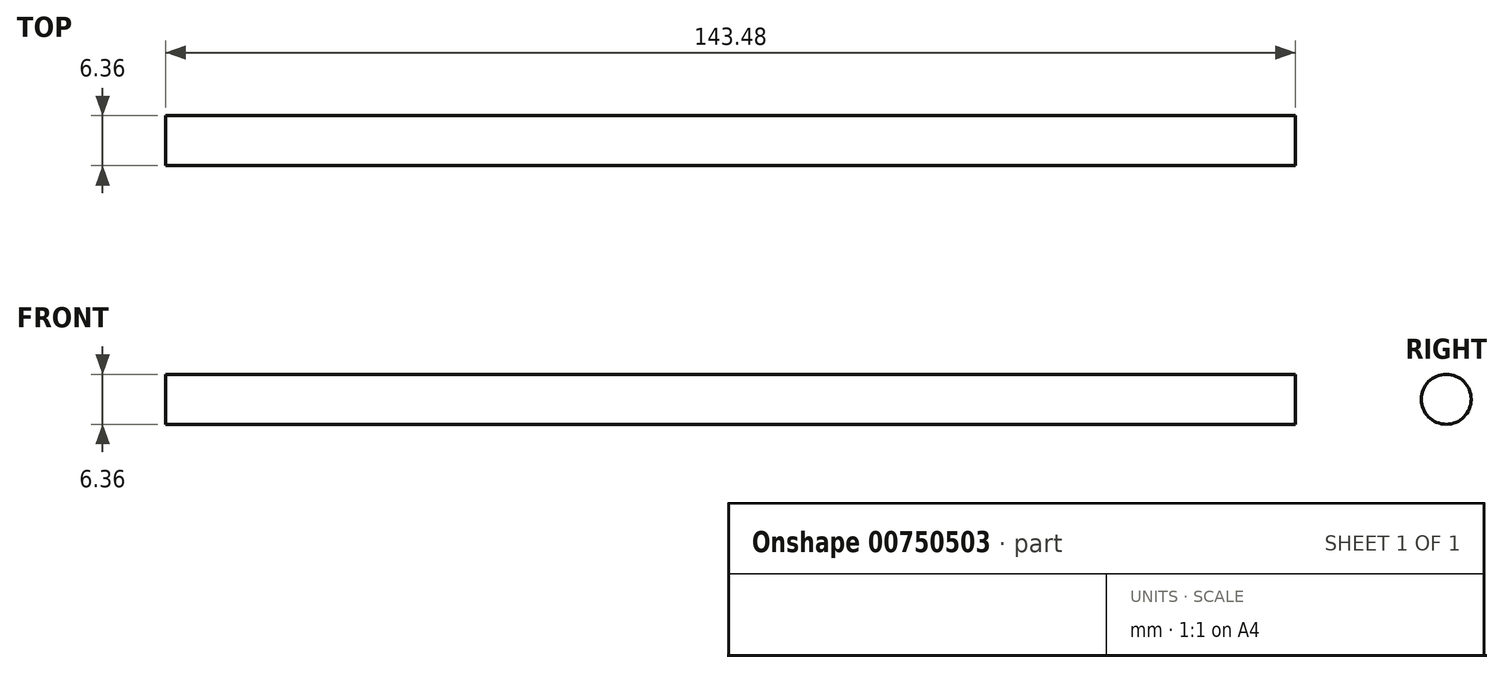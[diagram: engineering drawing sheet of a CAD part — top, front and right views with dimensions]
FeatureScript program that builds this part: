
annotation { "Feature Type Name" : "Feature", "Feature Type Description" : "" }
export const myFeature = defineFeature(function(context is Context, id is Id, definition is map)
    precondition{}
    {
        {
            var Q0;
            Q0=qCreatedBy(makeId("Right.planeOp"),FACE);
            var sketch = newSketch(context, id + "F0", { "sketchPlane" : qUnion([Q0])});
            skCircle(sketch, "E0", {"center": v(0, 0) * mm, "radius": 3.17 * mm});
            skSolve(sketch);
        }
        {
            var Q0;
            Q0=makeQuery(id+"F0.imprint","IMPRINT",FACE,{"disambiguationData":[TD([[makeQuery(id+"F0.imprint","IMPRINT",EDGE,{"derivedFrom":sQuery(id+"F0.wireOp",EDGE,"E0")}),1.0]])]});
            extrude(context, id + "F1", {"entities" : qUnion([Q0]), "endBound" : BoundingType.SYMMETRIC, "depth" : (914.4 / 4) * mm, "offsetDistance" : 25 * mm});
        }
        {
            var Q0;
            Q0=qCreatedBy(makeId("Top.planeOp"),FACE);
            var sketch = newSketch(context, id + "F2", { "sketchPlane" : qUnion([Q0])});
            skLineSegment(sketch, "E1.bottom", {"start": v(-121.07, 23.35) * mm, "end": v(-29.18, 23.35) * mm});
            skLineSegment(sketch, "E1.top", {"start": v(-121.07, -17.98) * mm, "end": v(-29.18, -17.98) * mm});
            skLineSegment(sketch, "E1.left", {"start": v(-121.07, 23.35) * mm, "end": v(-121.07, -17.98) * mm});
            skLineSegment(sketch, "E1.right", {"start": v(-29.18, 23.35) * mm, "end": v(-29.18, -17.98) * mm});
            skSolve(sketch);
        }
        {
            var Q0;
            Q0 = qSketchRegion(id + "F2", true);
            extrude(context, id + "F3", {"entities" : qUnion([Q0]), "operationType" : NewBodyOperationType.REMOVE, "endBound" : BoundingType.SYMMETRIC, "oppositeDirection" : true, "depth" : 25 * mm, "offsetDistance" : 25 * mm});
        }
    });
